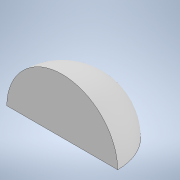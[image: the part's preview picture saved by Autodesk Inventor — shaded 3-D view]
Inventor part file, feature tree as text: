
AUTODESK INVENTOR PART (.ipt)
format: ipt  version: 2020 (Build 240168000, 168)  size: 109,056 bytes
history: native  units: mm
features: revolve x1, sketch x1
ambient origin geometry x8: Origin, YZ Plane, XZ Plane, XY Plane, X Axis, Y Axis, Z Axis, Center Point
bodies: Solid1 (feature_tree)
feature tree (2):
  revolve  "Revolution1"  [1 undecoded]
  sketch  "Sketch1"  dims[d0=0.99mm d1=1.0mm d2=1.0mm d3=180.0deg]
note: 1 required parameter value undecoded (feature->parameter linkage not recoverable at this tier; creation-order binding heuristic only, values carry confidence <= 0.55)
